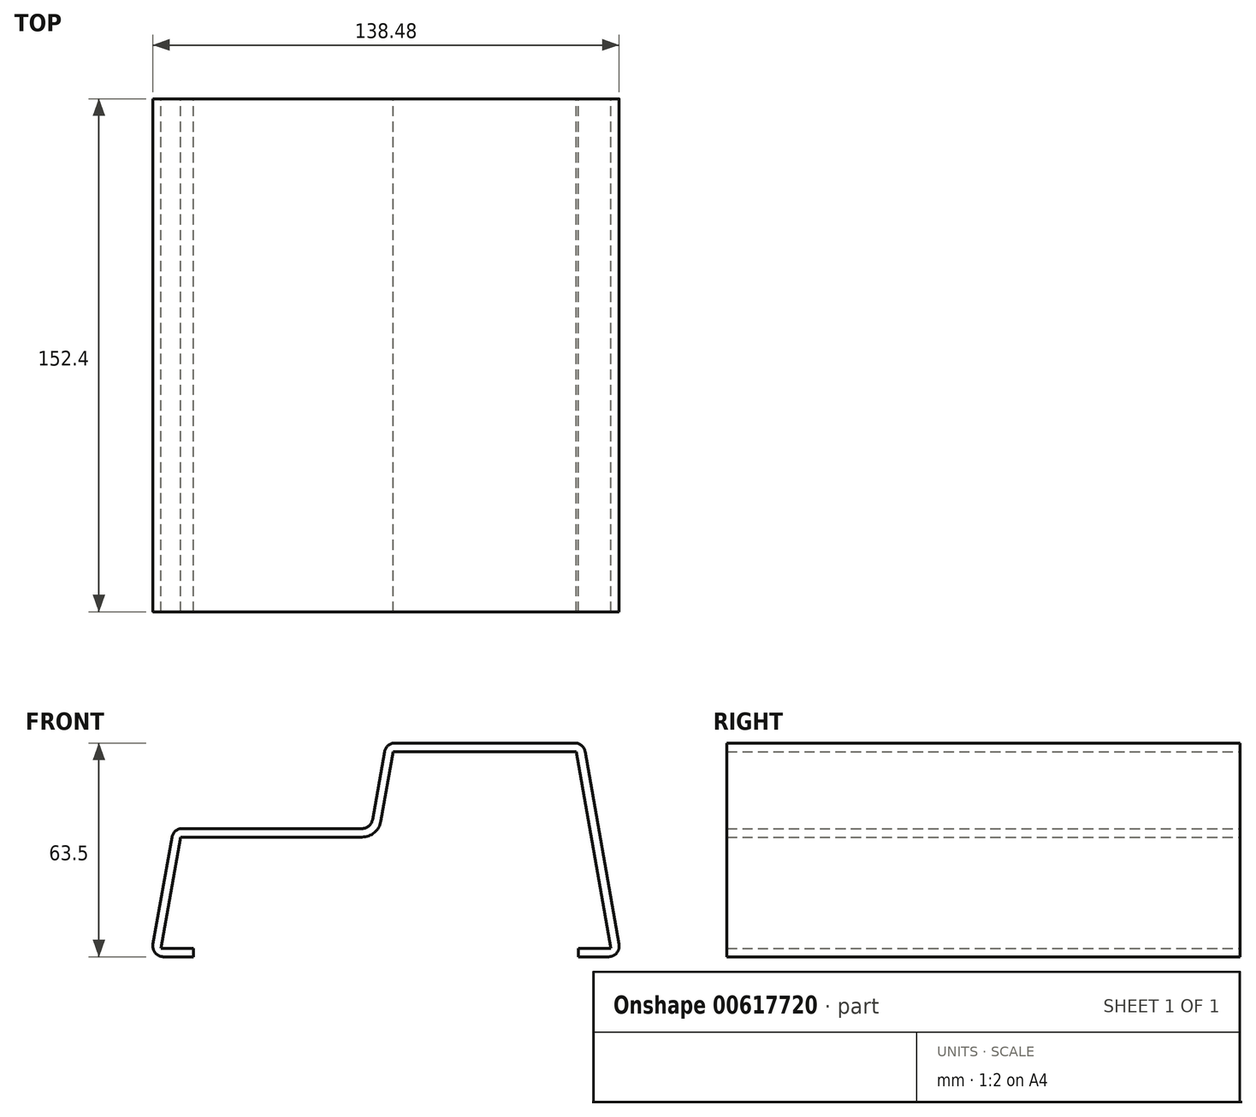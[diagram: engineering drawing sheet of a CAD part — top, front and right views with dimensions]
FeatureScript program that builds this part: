
annotation { "Feature Type Name" : "Feature", "Feature Type Description" : "" }
export const myFeature = defineFeature(function(context is Context, id is Id, definition is map)
    precondition{}
    {
        {
            var Q0;
            Q0=qCreatedBy(makeId("Front.planeOp"),FACE);
            var sketch = newSketch(context, id + "F0", { "sketchPlane" : qUnion([Q0])});
            skLineSegment(sketch, "E0", {"start": v(0, 0) * mm, "end": v(-8.92, 0) * mm});
            skLineSegment(sketch, "E1", {"start": v(-12.04, 3.73) * mm, "end": v(-6.44, 35.48) * mm});
            skLineSegment(sketch, "E2", {"start": v(-3.32, 38.1) * mm, "end": v(50, 38.1) * mm});
            skLineSegment(sketch, "E3", {"start": v(53.13, 40.72) * mm, "end": v(56.69, 60.88) * mm});
            skLineSegment(sketch, "E4", {"start": v(59.81, 63.5) * mm, "end": v(113.14, 63.5) * mm});
            skLineSegment(sketch, "E5", {"start": v(116.27, 60.88) * mm, "end": v(126.34, 3.73) * mm});
            skLineSegment(sketch, "E6", {"start": v(123.22, 0) * mm, "end": v(114.3, 0) * mm});
            skPoint(sketch, "E7.visualSharp", {"position": v(-12.7, 0) * mm});
            skArc(sketch, "E7.filletArc", {"start": v(-12.04, 3.73) * mm, "mid": v(-11.35, 1.13) * mm, "end": v(-8.92, 0) * mm});
            skPoint(sketch, "E8.visualSharp", {"position": v(-5.98, 38.1) * mm});
            skArc(sketch, "E8.filletArc", {"start": v(-3.32, 38.1) * mm, "mid": v(-5.36, 37.36) * mm, "end": v(-6.44, 35.48) * mm});
            skPoint(sketch, "E9.visualSharp", {"position": v(52.67, 38.1) * mm});
            skArc(sketch, "E9.filletArc", {"start": v(50, 38.1) * mm, "mid": v(52.05, 38.84) * mm, "end": v(53.13, 40.72) * mm});
            skPoint(sketch, "E10.visualSharp", {"position": v(57.15, 63.5) * mm});
            skArc(sketch, "E10.filletArc", {"start": v(59.81, 63.5) * mm, "mid": v(57.77, 62.76) * mm, "end": v(56.69, 60.88) * mm});
            skPoint(sketch, "E11.visualSharp", {"position": v(115.8, 63.5) * mm});
            skArc(sketch, "E11.filletArc", {"start": v(116.27, 60.88) * mm, "mid": v(115.18, 62.76) * mm, "end": v(113.14, 63.5) * mm});
            skPoint(sketch, "E12.visualSharp", {"position": v(127, 0) * mm});
            skArc(sketch, "E12.filletArc", {"start": v(123.22, 0) * mm, "mid": v(125.65, 1.13) * mm, "end": v(126.34, 3.73) * mm});
            skLineSegment(sketch, "E13.0", {"start": v(123.97, 2.54) * mm, "end": v(114.3, 2.54) * mm});
            skLineSegment(sketch, "E13.1", {"start": v(113.67, 60.96) * mm, "end": v(123.97, 2.54) * mm});
            skLineSegment(sketch, "E13.2", {"start": v(59.28, 60.96) * mm, "end": v(113.67, 60.96) * mm});
            skLineSegment(sketch, "E13.3", {"start": v(55.64, 40.28) * mm, "end": v(59.28, 60.96) * mm});
            skLineSegment(sketch, "E13.4", {"start": v(0, 2.54) * mm, "end": v(-9.67, 2.54) * mm});
            skLineSegment(sketch, "E13.5", {"start": v(-9.67, 2.54) * mm, "end": v(-3.85, 35.56) * mm});
            skLineSegment(sketch, "E13.6", {"start": v(-3.85, 35.56) * mm, "end": v(50, 35.56) * mm});
            skArc(sketch, "E13.7", {"start": v(50, 35.56) * mm, "mid": v(53.68, 36.9) * mm, "end": v(55.64, 40.28) * mm});
            skLineSegment(sketch, "E14", {"start": v(0, 2.54) * mm, "end": v(0, 0) * mm});
            skLineSegment(sketch, "E15", {"start": v(114.3, 2.54) * mm, "end": v(114.3, 0) * mm});
            skSolve(sketch);
        }
        {
            var Q0;
            Q0 = qSketchRegion(id + "F0", true);
            extrude(context, id + "F1", {"entities" : qUnion([Q0]), "depth" : 152.4 * mm, "offsetDistance" : 25.4 * mm});
        }
    });
